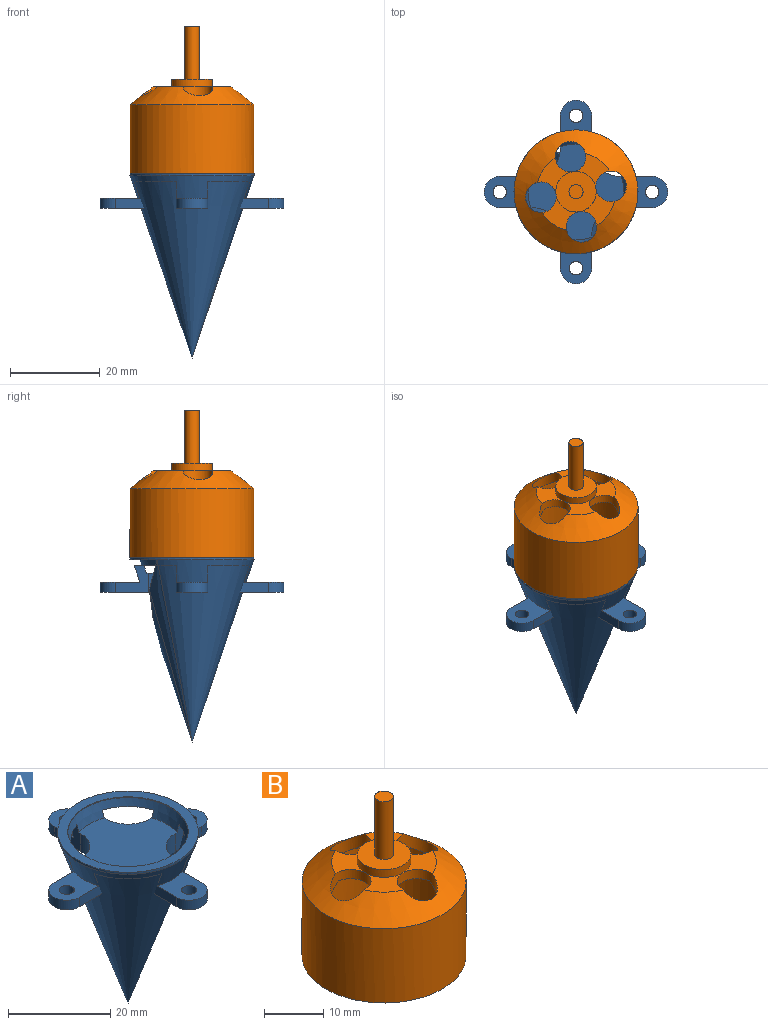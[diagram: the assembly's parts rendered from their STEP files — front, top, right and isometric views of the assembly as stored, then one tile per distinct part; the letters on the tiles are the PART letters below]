
ASSEMBLY  parts=2 mates=1
PART A: 36 faces, bbox 40.9x40.9x7.8 mm
  f0: cone r=12.1mm half-angle=18.8deg, axis (0,0,1), area 0.7mm2, adj f1,f2,f3,f4
  f1: cylinder r=13.8mm len=27.6mm, axis (0,0,1), area 43.4mm2, adj f0,f5
  f2: cone r=12.1mm half-angle=18.8deg, axis (0,0,1), area 196.3mm2, adj f0,f3,f6,f7,f8,f9,f10,f11
  f3: plane 8.87x7mm, normal (0,0,1), area 47.3mm2, adj f0,f2,f4,f8,f20,f21
  f4: plane 7.31x5.92mm, normal (0,1,0), area 24.9mm2, adj f0,f3,f7,f21,f22,f23,f24,f25
  f5: plane 27.6x27.6mm, normal (0,0,1), area 160.8mm2, adj f1,f26
  f6: plane 7.31x5.92mm, normal (1,0,0), area 24.9mm2, adj f2,f7,f19,f22,f23,f24,f25,f27
  f7: plane 9.36x9.36mm, normal (0,0,-1), area 25.7mm2, adj f2,f4,f6,f25
  f8: plane 7.31x5.92mm, normal (0,-1,0), area 24.9mm2, adj f2,f3,f9,f21,f22,f24,f25,f28
  f9: plane 9.36x9.36mm, normal (0,0,-1), area 25.7mm2, adj f2,f8,f10,f25
  f10: plane 7.31x5.92mm, normal (1,0,0), area 24.9mm2, adj f2,f9,f11,f22,f24,f25,f28,f29
  f11: plane 8.87x7mm, normal (0,0,1), area 47.3mm2, adj f2,f10,f12,f29,f30
  f12: plane 7.31x5.92mm, normal (-1,0,0), area 24.9mm2, adj f2,f11,f13,f22,f24,f25,f29,f31
  f13: plane 9.36x9.36mm, normal (0,0,-1), area 25.7mm2, adj f2,f12,f14,f25
  f14: plane 7.31x5.92mm, normal (0,-1,0), area 24.9mm2, adj f2,f13,f15,f22,f24,f25,f31,f32
  f15: plane 8.87x7mm, normal (0,0,1), area 47.3mm2, adj f2,f14,f16,f32,f33
  f16: plane 7.31x5.92mm, normal (0,1,0), area 24.9mm2, adj f2,f15,f17,f22,f24,f25,f32,f34
  f17: plane 9.36x9.36mm, normal (0,0,-1), area 25.7mm2, adj f2,f16,f18,f25
  f18: plane 7.31x5.92mm, normal (-1,0,0), area 24.9mm2, adj f2,f17,f19,f22,f24,f25,f27,f34
  f19: plane 8.87x7mm, normal (0,0,1), area 47.3mm2, adj f2,f6,f18,f27,f35
  f20: cylinder r=1.5mm len=3mm, axis (0,0,1), area 21.7mm2, adj f3,f22
  f21: cylinder r=3.5mm len=7mm, axis (0,0,1), area 25.3mm2, adj f3,f4,f8,f22
  f22: plane 40.9x40.9mm, normal (0,0,-1), area 506.8mm2, adj f4,f6,f8,f10,f12,f14,f16,f18
  f23: cylinder r=6.16mm len=6.16mm, axis (0,0,-1), area 41.6mm2, adj f4,f6,f22,f24
  f24: plane 21.34x21.34mm, normal (0,0,1), area 276.8mm2, adj f4,f6,f8,f10,f12,f14,f16,f18
  f25: cone r=10.21mm half-angle=18.8deg, axis (0,0,1), area 180.3mm2, adj f4,f6,f7,f8,f9,f10,f12,f13
  f26: cylinder r=11.8mm len=23.6mm, axis (0,0,1), area 12.6mm2, adj f5,f25
  f27: cylinder r=3.5mm len=7mm, axis (0,0,1), area 25.3mm2, adj f6,f18,f19,f22
  f28: cylinder r=6.16mm len=6.16mm, axis (0,0,-1), area 41.6mm2, adj f8,f10,f22,f24
  f29: cylinder r=3.5mm len=7mm, axis (0,0,1), area 25.3mm2, adj f10,f11,f12,f22
  f30: cylinder r=1.5mm len=3mm, axis (0,0,1), area 21.7mm2, adj f11,f22
  f31: cylinder r=6.16mm len=6.16mm, axis (0,0,-1), area 41.6mm2, adj f12,f14,f22,f24
  f32: cylinder r=3.5mm len=7mm, axis (0,0,1), area 25.3mm2, adj f14,f15,f16,f22
  f33: cylinder r=1.5mm len=3mm, axis (0,0,1), area 21.7mm2, adj f15,f22
  f34: cylinder r=6.16mm len=6.16mm, axis (0,0,-1), area 41.6mm2, adj f16,f18,f22,f24
  f35: cylinder r=1.5mm len=3mm, axis (0,0,1), area 21.7mm2, adj f19,f22
PART B: 20 faces, bbox 27.6x27.6x32.8 mm
  f0: plane 8.12x8.12mm, normal (0,0,1), area 22.2mm2, adj f6,f7,f18,f19
  f1: plane 8.12x8.12mm, normal (0,0,1), area 22.2mm2, adj f6,f7,f17,f18
  f2: plane 8.12x8.12mm, normal (0,0,1), area 22.2mm2, adj f6,f7,f16,f17
  f3: cylinder r=13.8mm len=27.6mm, axis (0,0,1), area 1326.6mm2, adj f4,f6
  f4: plane 27.6x27.6mm, normal (0,0,-1), area 153.4mm2, adj f3,f11
  f5: plane 8.12x8.12mm, normal (0,0,1), area 22.2mm2, adj f6,f7,f16,f19
  f6: cone r=8.8mm half-angle=51.3deg, axis (0,0,-1), area 385.2mm2, adj f0,f1,f2,f3,f5,f16,f17,f18
  f7: cylinder r=4.5mm len=9mm, axis (0,0,-1), area 45.2mm2, adj f0,f1,f2,f5,f8
  f8: plane 9x9mm, normal (0,0,1), area 55.9mm2, adj f7,f9
  f9: cylinder r=1.57mm len=11.9mm, axis (0,0,-1), area 117.4mm2, adj f8,f10
  f10: plane 3.14x3.14mm, normal (0,0,1), area 7.7mm2, adj f9
  f11: cylinder r=11.9mm len=23.8mm, axis (0,0,1), area 1075.7mm2, adj f4,f13
  f12: plane 14.81x14.81mm, normal (0,0,-1), area 114.2mm2, adj f13,f14,f16,f17,f18,f19
  f13: cone r=7.61mm half-angle=51.3deg, axis (0,0,-1), area 210.3mm2, adj f11,f12,f16,f17,f18,f19
  f14: cylinder r=2.6mm len=5.2mm, axis (0,0,-1), area 26.1mm2, adj f12,f15
  f15: plane 5.2x5.2mm, normal (0,0,-1), area 21.2mm2, adj f14
  f16: cylinder r=3.4mm len=6.8mm, axis (0,0,1), area 46.4mm2, adj f2,f5,f6,f12,f13
  f17: cylinder r=3.4mm len=6.8mm, axis (0,0,1), area 46.4mm2, adj f1,f2,f6,f12,f13
  f18: cylinder r=3.4mm len=6.8mm, axis (0,0,1), area 46.4mm2, adj f0,f1,f6,f12,f13
  f19: cylinder r=3.4mm len=6.8mm, axis (0,0,1), area 46.4mm2, adj f0,f5,f6,f12,f13
PLACE A t=(0,0,0.4)mm fixed
PLACE B rot(axis=(0,0,-1),171.2deg) t=(0,0,0)mm
MATE revolute A.f0 <-> B.f3  axis (0,0,1) through (0,0,-19.3)mm
